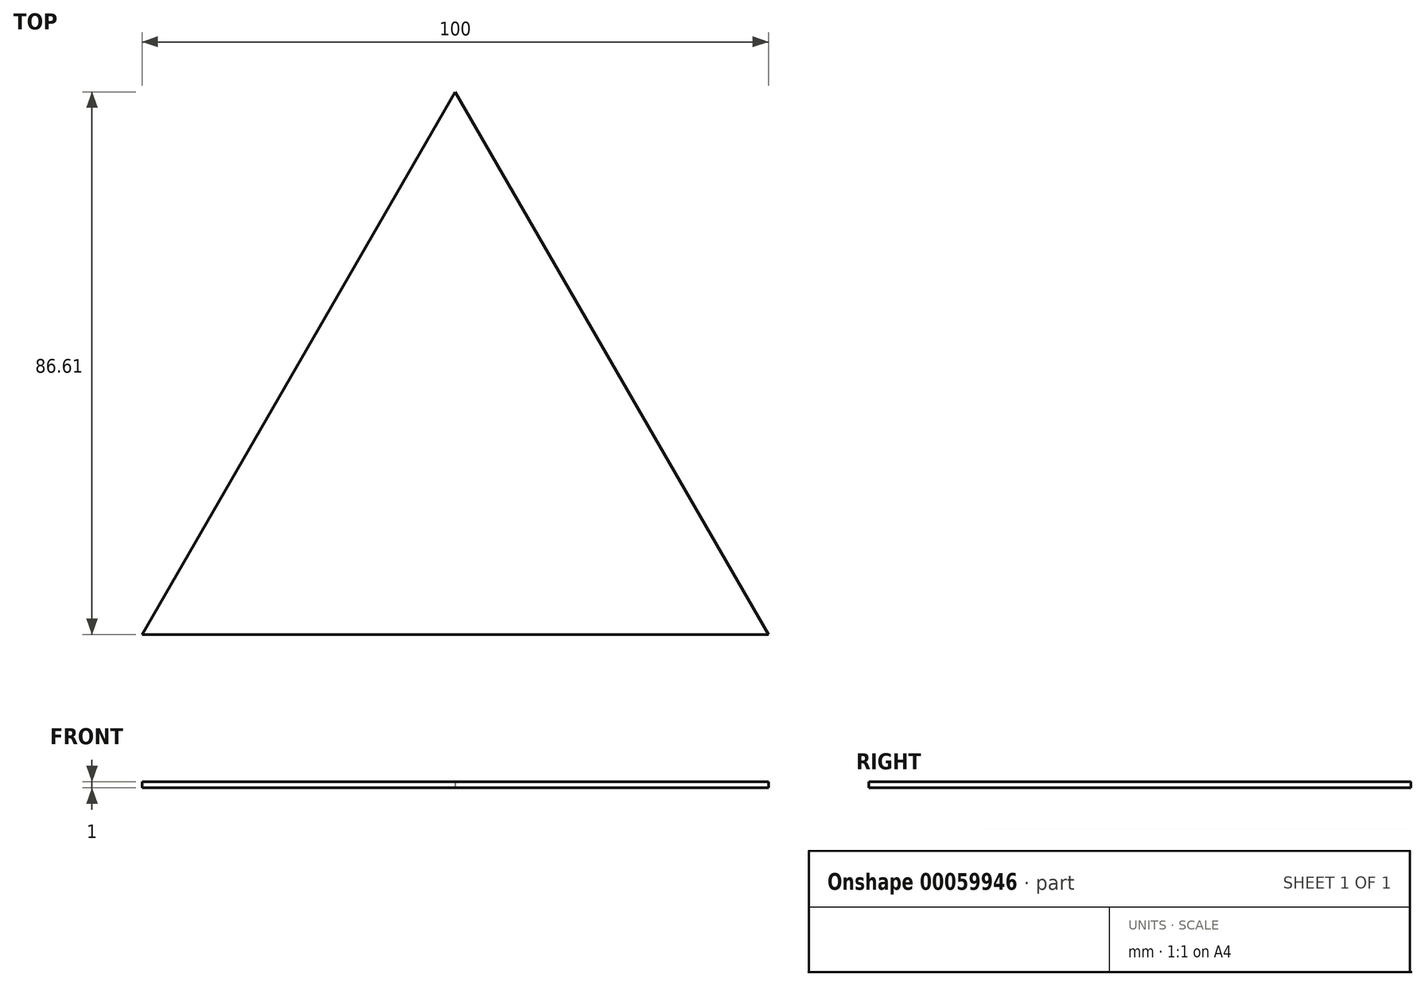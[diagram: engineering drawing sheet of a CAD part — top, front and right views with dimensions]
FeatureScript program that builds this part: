
annotation { "Feature Type Name" : "Feature", "Feature Type Description" : "" }
export const myFeature = defineFeature(function(context is Context, id is Id, definition is map)
    precondition{}
    {
        {
            var Q0;
            Q0=qCreatedBy(makeId("Top.planeOp"),FACE);
            var sketch = newSketch(context, id + "F0", { "sketchPlane" : qUnion([Q0])});
            skLineSegment(sketch, "E0.0", {"start": v(0, 57.74) * mm, "end": v(50, -28.87) * mm});
            skLineSegment(sketch, "E0.1", {"start": v(50, -28.87) * mm, "end": v(-50, -28.87) * mm});
            skLineSegment(sketch, "E0.2", {"start": v(-50, -28.87) * mm, "end": v(0, 57.74) * mm});
            skSolve(sketch);
        }
        {
            var Q0;
            Q0=makeQuery(id+"F0.imprint","IMPRINT",FACE,{"disambiguationData":[TD([[makeQuery(id+"F0.imprint","IMPRINT",EDGE,{"derivedFrom":sQuery(id+"F0.wireOp",EDGE,"E0.0")}),-1.0]])]});
            extrude(context, id + "F1", {"entities" : qUnion([Q0]), "depth" : 1 * mm});
        }
    });
